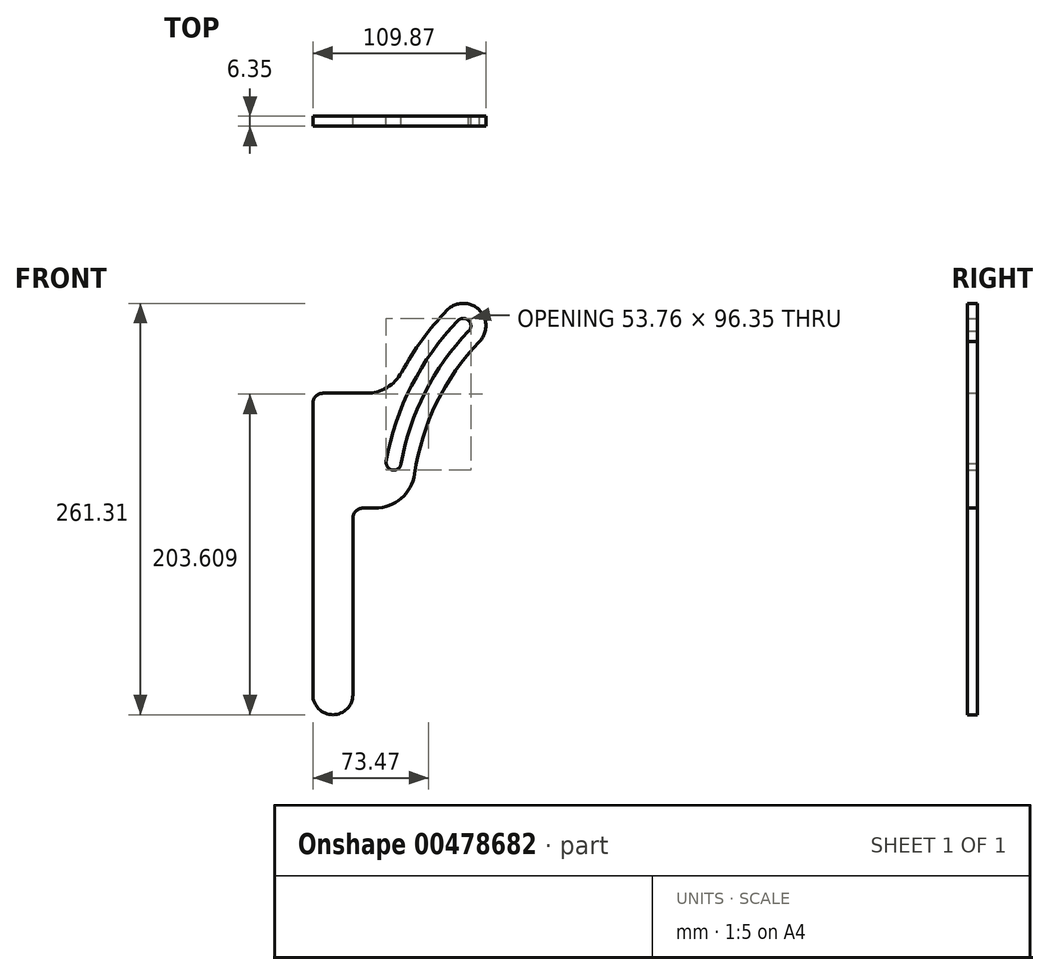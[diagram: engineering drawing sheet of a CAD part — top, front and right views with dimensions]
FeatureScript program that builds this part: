
annotation { "Feature Type Name" : "Feature", "Feature Type Description" : "" }
export const myFeature = defineFeature(function(context is Context, id is Id, definition is map)
    precondition{}
    {
        {
            var Q0;
            Q0=qCreatedBy(makeId("Front.planeOp"),FACE);
            var sketch = newSketch(context, id + "F0", { "sketchPlane" : qUnion([Q0])});
            skPoint(sketch, "E0", {"position": v(0, 0) * mm});
            skLineSegment(sketch, "E1", {"start": v(0, 0) * mm, "end": v(0, 186.11) * mm, "construction": true});
            skLineSegment(sketch, "E2.0", {"start": v(41.28, 0) * mm, "end": v(41.28, 143.5) * mm, "construction": true});
            skPoint(sketch, "E3", {"position": v(41.28, 159.86) * mm});
            skPoint(sketch, "E4.orphan", {"position": v(-82.55, 319.71) * mm});
            skPoint(sketch, "E5", {"position": v(74.62, 224.66) * mm});
            skPoint(sketch, "E6", {"position": v(-174.62, 159.86) * mm});
            skArc(sketch, "E7", {"start": v(86.24, 237.7) * mm, "mid": v(54.24, 194.19) * mm, "end": v(37.83, 142.73) * mm, "construction": true});
            skPoint(sketch, "E8.orphan", {"position": v(201.13, 283.68) * mm});
            skArc(sketch, "E9.0", {"start": v(79.44, 237.63) * mm, "mid": v(49.99, 196.36) * mm, "end": v(33.9, 148.27) * mm});
            skPoint(sketch, "E10", {"position": v(82.87, 234.31) * mm});
            skPoint(sketch, "E11", {"position": v(38.6, 147.44) * mm});
            skArc(sketch, "E12", {"start": v(33.9, 148.27) * mm, "mid": v(37.82, 142.73) * mm, "end": v(43.31, 146.72) * mm});
            skArc(sketch, "E13", {"start": v(86.23, 230.92) * mm, "mid": v(86.23, 237.7) * mm, "end": v(79.44, 237.63) * mm});
            skArc(sketch, "E14", {"start": v(43.28, 146.5) * mm, "mid": v(58.5, 192.02) * mm, "end": v(86.38, 231.07) * mm});
            skCircle(sketch, "E15", {"center": v(0, 0) * mm, "radius": 12.7 * mm});
            skArc(sketch, "E16.0", {"start": v(72.6, 244.25) * mm, "mid": v(56.78, 225.5) * mm, "end": v(43.65, 204.78) * mm});
            skArc(sketch, "E17.0", {"start": v(93.03, 224.24) * mm, "mid": v(93.13, 224.35) * mm, "end": v(93.23, 224.45) * mm});
            skArc(sketch, "E18", {"start": v(72.6, 244.25) * mm, "mid": v(92.88, 244.53) * mm, "end": v(93.03, 224.24) * mm});
            skPoint(sketch, "E19.visualSharp", {"position": v(23.7, 144.86) * mm});
            skArc(sketch, "E20", {"start": v(93.23, 224.45) * mm, "mid": v(65.94, 185.61) * mm, "end": v(51.92, 140.27) * mm});
            skLineSegment(sketch, "E21", {"start": v(12.7, 0) * mm, "end": v(12.7, 112.14) * mm});
            skLineSegment(sketch, "E22", {"start": v(19.05, 118.5) * mm, "end": v(26.78, 118.5) * mm});
            skPoint(sketch, "E23.visualSharp", {"position": v(50.36, 118.5) * mm});
            skArc(sketch, "E23.filletArc", {"start": v(26.78, 118.5) * mm, "mid": v(43.41, 124.7) * mm, "end": v(51.92, 140.27) * mm});
            skPoint(sketch, "E24.visualSharp", {"position": v(12.7, 118.5) * mm});
            skArc(sketch, "E24.filletArc", {"start": v(19.05, 118.5) * mm, "mid": v(14.56, 116.63) * mm, "end": v(12.7, 112.14) * mm});
            skLineSegment(sketch, "E25", {"start": v(-12.7, 0) * mm, "end": v(-12.7, 185.14) * mm});
            skLineSegment(sketch, "E26", {"start": v(-6.35, 191.49) * mm, "end": v(21.33, 191.49) * mm});
            skArc(sketch, "E27.filletArc", {"start": v(21.33, 191.49) * mm, "mid": v(34.32, 195.06) * mm, "end": v(43.65, 204.78) * mm});
            skPoint(sketch, "E28.visualSharp", {"position": v(-12.7, 191.49) * mm});
            skArc(sketch, "E28.filletArc", {"start": v(-6.35, 191.49) * mm, "mid": v(-10.84, 189.63) * mm, "end": v(-12.7, 185.14) * mm});
            skSolve(sketch);
        }
        {
            var Q0;
            Q0 = qSketchRegion(id + "F0", true);
            extrude(context, id + "F1", {"entities" : qUnion([Q0]), "depth" : 6.35 * mm, "offsetDistance" : 25.4 * mm});
        }
    });
